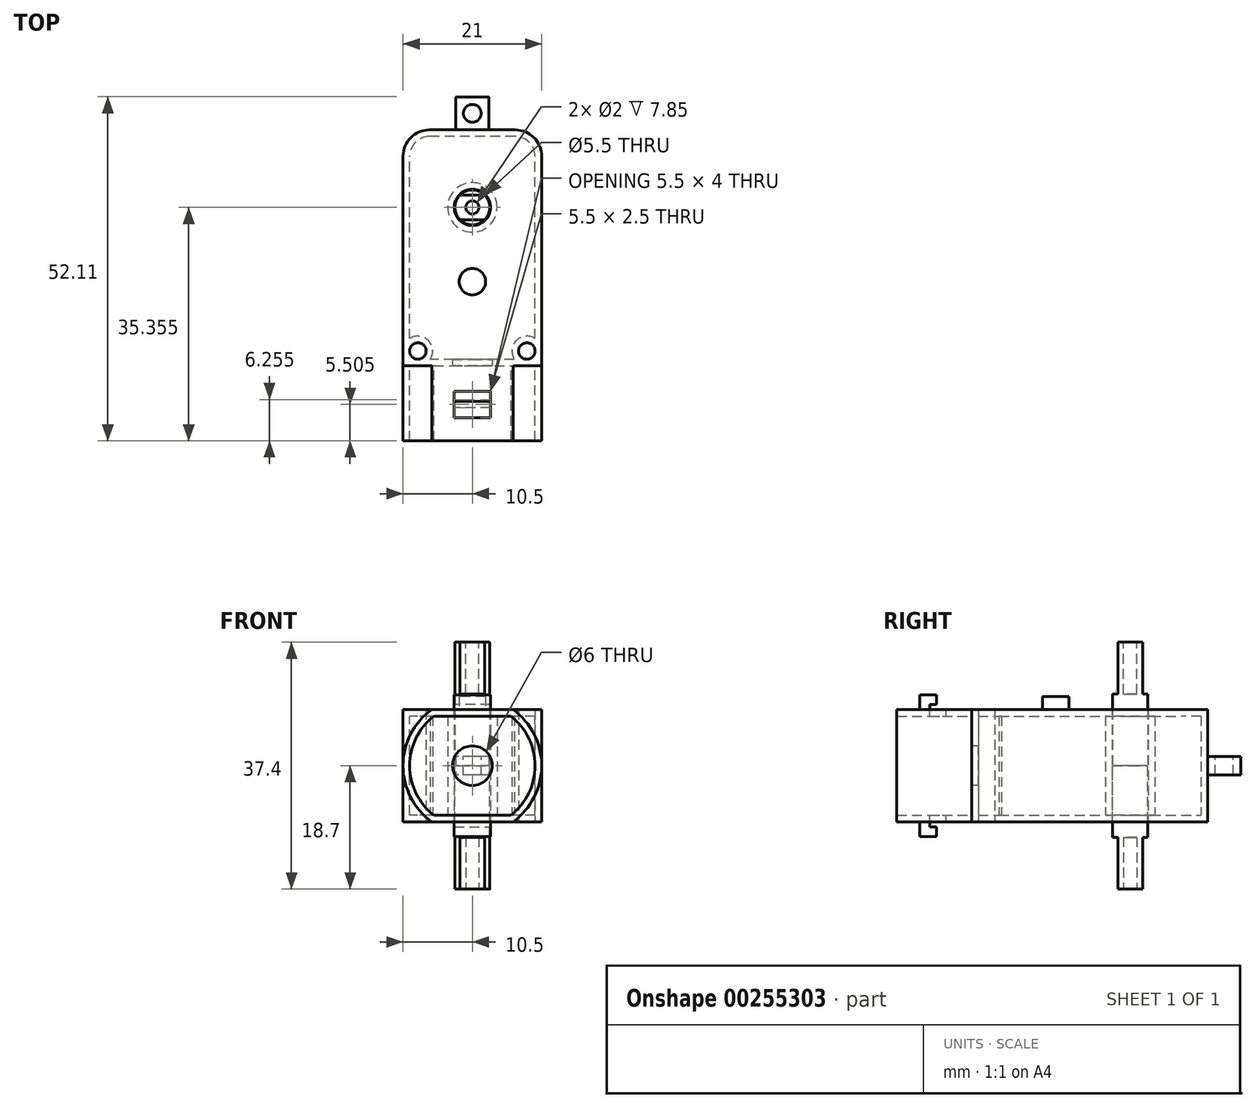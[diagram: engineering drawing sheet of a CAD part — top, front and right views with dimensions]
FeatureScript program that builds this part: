
annotation { "Feature Type Name" : "Feature", "Feature Type Description" : "" }
export const myFeature = defineFeature(function(context is Context, id is Id, definition is map)
    precondition{}
    {
        {
            var Q0;
            Q0=qCreatedBy(makeId("Top.planeOp"),FACE);
            var sketch = newSketch(context, id + "F0", { "sketchPlane" : qUnion([Q0])});
            skLineSegment(sketch, "E0.bottom", {"start": v(10.5, -17.88) * mm, "end": v(-10.5, -17.88) * mm});
            skLineSegment(sketch, "E0.top", {"start": v(10.5, 17.88) * mm, "end": v(-10.5, 17.88) * mm});
            skLineSegment(sketch, "E0.left", {"start": v(10.5, -17.88) * mm, "end": v(10.5, 17.88) * mm});
            skLineSegment(sketch, "E0.right", {"start": v(-10.5, -17.88) * mm, "end": v(-10.5, 17.88) * mm});
            skPoint(sketch, "E0.middle", {"position": v(0, 0) * mm});
            skCircle(sketch, "E1", {"center": v(0, 6.12) * mm, "radius": 2.75 * mm});
            skLineSegment(sketch, "E2", {"start": v(0, 8.88) * mm, "end": v(0, 17.88) * mm});
            skCircle(sketch, "E3", {"center": v(0, -5.13) * mm, "radius": 2 * mm});
            skLineSegment(sketch, "E4", {"start": v(0, 3.37) * mm, "end": v(0, -3.13) * mm});
            skCircle(sketch, "E5", {"center": v(-8.25, -15.63) * mm, "radius": 1.25 * mm});
            skLineSegment(sketch, "E6", {"start": v(-8.25, -16.88) * mm, "end": v(-8.25, -17.88) * mm});
            skLineSegment(sketch, "E7", {"start": v(-9.5, -15.63) * mm, "end": v(-10.5, -15.63) * mm});
            skLineSegment(sketch, "E8", {"start": v(0, -7.13) * mm, "end": v(0, -17.88) * mm});
            skCircle(sketch, "E9.MirrorC", {"center": v(8.25, -15.62) * mm, "radius": 1.25 * mm});
            skSolve(sketch);
        }
        {
            var Q0;
            {var subQ3=sQuery(id+"F0.wireOp",EDGE,"E2");Q0=makeQuery(id+"F0.imprint","IMPRINT",FACE,{"disambiguationData":[TD([[makeQuery(id+"F0.imprint","IMPRINT",EDGE,{"derivedFrom":subQ3}),1.0]])]});}
            var Q1;
            {var subQ3=sQuery(id+"F0.wireOp",EDGE,"E0.left");Q1=makeQuery(id+"F0.imprint","IMPRINT",FACE,{"disambiguationData":[TD([[makeQuery(id+"F0.imprint","IMPRINT",EDGE,{"derivedFrom":subQ3}),1.0]])]});}
            var Q2;
            {var subQ0=sQuery(id+"F0.wireOp",EDGE,"E6");Q2=makeQuery(id+"F0.imprint","IMPRINT",FACE,{"disambiguationData":[TD([[makeQuery(id+"F0.imprint","IMPRINT",EDGE,{"derivedFrom":subQ0}),-1.0]])]});}
            var Q3;
            {var subQ0=sQuery(id+"F0.wireOp",EDGE,"E3");var subQ1=makeQuery(id+"F0.imprint","INTERSECT",VERTEX,{"derivedFrom":[subQ0,sQuery(id+"F0.wireOp",EDGE,"E4")]});Q3=makeQuery(id+"F0.imprint","IMPRINT",FACE,{"disambiguationData":[TD([[makeQuery(id+"F0.imprint","IMPRINT",EDGE,{"disambiguationData":[TD([[subQ1,-1.0]])],"derivedFrom":subQ0}),1.0]])]});}
            extrude(context, id + "F1", {"entities" : qUnion([Q0, Q1, Q2, Q3]), "endBound" : BoundingType.SYMMETRIC, "depth" : 17 * mm});
        }
        {
            var Q0;
            Q0=makeQuery(id+"F1.opExtrude","SWEPT_EDGE",EDGE,{"disambiguationData":[OSD([sQuery(id+"F0.wireOp",EDGE,"E0.top"),sQuery(id+"F0.wireOp",EDGE,"E0.right")])]});
            var Q1;
            Q1=makeQuery(id+"F1.opExtrude","SWEPT_EDGE",EDGE,{"disambiguationData":[OSD([sQuery(id+"F0.wireOp",EDGE,"E0.top"),sQuery(id+"F0.wireOp",EDGE,"E0.left")])]});
            fillet(context, id + "F2", {"entities" : qUnion([Q0, Q1]), "radius" : 4 * mm, "tangentPropagation" : true, "allowEdgeOverflow" : false});
        }
        {
            var Q0;
            Q0=makeQuery(id+"F1.opExtrude","SWEPT_FACE",FACE,{"disambiguationData":[OSD([sQuery(id+"F0.wireOp",EDGE,"E1")])]});
            var Q1;
            Q1=makeQuery(id+"F1.opExtrude","SWEPT_BODY",BODY,{"disambiguationData":[OSD([sQuery(id+"F0.wireOp",EDGE,"E0.bottom"),sQuery(id+"F0.wireOp",EDGE,"E0.top"),sQuery(id+"F0.wireOp",EDGE,"E0.left"),sQuery(id+"F0.wireOp",EDGE,"E0.right"),sQuery(id+"F0.wireOp",EDGE,"E1"),sQuery(id+"F0.wireOp",EDGE,"E3"),sQuery(id+"F0.wireOp",EDGE,"E5"),sQuery(id+"F0.wireOp",EDGE,"E9.MirrorC")])]});
            shell(context, id + "F3", {"isHollow" : true, "entities" : qUnion([Q0]), "parts" : qUnion([Q1]), "thickness" : 1 * mm});
        }
        {
            var Q0;
            Q0=makeQuery(id+"F1.opExtrude","SWEPT_FACE",FACE,{"disambiguationData":[OSD([sQuery(id+"F0.wireOp",EDGE,"E0.top")])]});
            var sketch = newSketch(context, id + "F4", { "sketchPlane" : qUnion([Q0])});
            skLineSegment(sketch, "E10.bottom", {"start": v(-2.5, 1.4) * mm, "end": v(2.5, 1.4) * mm});
            skLineSegment(sketch, "E10.top", {"start": v(-2.5, -1.4) * mm, "end": v(2.5, -1.4) * mm});
            skLineSegment(sketch, "E10.left", {"start": v(-2.5, 1.4) * mm, "end": v(-2.5, -1.4) * mm});
            skLineSegment(sketch, "E10.right", {"start": v(2.5, 1.4) * mm, "end": v(2.5, -1.4) * mm});
            skPoint(sketch, "E10.middle", {"position": v(0, 0) * mm});
            skSolve(sketch);
        }
        {
            var Q0;
            Q0=qSketchRegion(id+"F4",true);
            extrude(context, id + "F5", {"entities" : qUnion([Q0]), "operationType" : NewBodyOperationType.ADD, "depth" : 5 * mm});
        }
        {
            var Q0;
            Q0=makeQuery(id+"F5.opExtrude","CAP_EDGE",EDGE,{"disambiguationData":[OSD([sQuery(id+"F4.wireOp",EDGE,"E10.right")])],"isStart":false});
            var Q1;
            Q1=makeQuery(id+"F5.opExtrude","CAP_EDGE",EDGE,{"disambiguationData":[OSD([sQuery(id+"F4.wireOp",EDGE,"E10.left")])],"isStart":false});
            var Q2;
            Q2=makeQuery(id+"F5.opExtrude","CAP_EDGE",EDGE,{"disambiguationData":[OSD([sQuery(id+"F4.wireOp",EDGE,"E10.left")])],"isStart":true});
            var Q3;
            Q3=makeQuery(id+"F5.opExtrude","CAP_EDGE",EDGE,{"disambiguationData":[OSD([sQuery(id+"F4.wireOp",EDGE,"E10.right")])],"isStart":true});
            fillet(context, id + "F6", {"entities" : qUnion([Q0, Q1, Q2, Q3]), "radius" : (1 / 8) * mm, "tangentPropagation" : true, "allowEdgeOverflow" : false});
        }
        {
            var Q0;
            Q0=makeQuery(id+"F5.opExtrude","SWEPT_FACE",FACE,{"disambiguationData":[OSD([sQuery(id+"F4.wireOp",EDGE,"E10.bottom")])]});
            var sketch = newSketch(context, id + "F7", { "sketchPlane" : qUnion([Q0])});
            skCircle(sketch, "E11", {"center": v(0, 20.38) * mm, "radius": 1.35 * mm});
            skPoint(sketch, "E11.centerSnap0", {"position": v(-2.5, 20.38) * mm});
            skSolve(sketch);
        }
        {
            var Q0;
            Q0=qSketchRegion(id+"F7",true);
            extrude(context, id + "F8", {"entities" : qUnion([Q0]), "operationType" : NewBodyOperationType.REMOVE, "oppositeDirection" : true, "depth" : 2.8 * mm});
        }
        {
            var Q0;
            Q0=makeQuery(id+"F1.opExtrude","SWEPT_FACE",FACE,{"disambiguationData":[OSD([sQuery(id+"F0.wireOp",EDGE,"E0.bottom")])]});
            var sketch = newSketch(context, id + "F9", { "sketchPlane" : qUnion([Q0])});
            skArc(sketch, "E12", {"start": v(-6.16, 8.5) * mm, "mid": v(-10.5, 0) * mm, "end": v(-6.16, -8.5) * mm});
            skLineSegment(sketch, "E13", {"start": v(-6.16, 8.5) * mm, "end": v(6.16, 8.5) * mm});
            skLineSegment(sketch, "E14", {"start": v(-6.16, -8.5) * mm, "end": v(6.16, -8.5) * mm});
            skArc(sketch, "E15.trimOffspring", {"start": v(6.16, -8.5) * mm, "mid": v(10.5, 0) * mm, "end": v(6.16, 8.5) * mm});
            skArc(sketch, "E16", {"start": v(4.24, -8.5) * mm, "mid": v(9.5, 0) * mm, "end": v(4.24, 8.5) * mm});
            skLineSegment(sketch, "E17", {"start": v(-4.24, 8.5) * mm, "end": v(4.24, 8.5) * mm});
            skLineSegment(sketch, "E18", {"start": v(-4.24, -8.5) * mm, "end": v(4.24, -8.5) * mm});
            skArc(sketch, "E19.trimOffspring", {"start": v(-4.24, 8.5) * mm, "mid": v(-9.5, 0) * mm, "end": v(-4.24, -8.5) * mm});
            skLineSegment(sketch, "E20", {"start": v(-5.83, 7.5) * mm, "end": v(5.83, 7.5) * mm});
            skLineSegment(sketch, "E21", {"start": v(-5.83, -7.5) * mm, "end": v(5.83, -7.5) * mm});
            skLineSegment(sketch, "E22", {"start": v(-1.98, -7.5) * mm, "end": v(-1.98, -8.5) * mm});
            skLineSegment(sketch, "E23", {"start": v(-2.47, 7.5) * mm, "end": v(-2.47, 8.5) * mm});
            skSolve(sketch);
        }
        {
            var Q0;
            Q0=qSketchRegion(id+"F9",true);
            extrude(context, id + "F10", {"entities" : qUnion([Q0]), "operationType" : NewBodyOperationType.ADD, "depth" : 11.35 * mm});
        }
        {
            var Q0;
            Q0=makeQuery(id+"F10.boolean.opBoolean","SPLIT",FACE,{"disambiguationData":[TD([makeQuery(id+"F10.opExtrude","SWEPT_FACE",FACE,{"disambiguationData":[OSD([sQuery(id+"F9.wireOp",EDGE,"E16")])]}),makeQuery(id+"F10.opExtrude","SWEPT_FACE",FACE,{"disambiguationData":[OSD([sQuery(id+"F9.wireOp",EDGE,"E19.trimOffspring")])]}),makeQuery(id+"F10.opExtrude","SWEPT_FACE",FACE,{"disambiguationData":[OSD([sQuery(id+"F9.wireOp",EDGE,"E20")])]}),makeQuery(id+"F10.opExtrude","SWEPT_FACE",FACE,{"disambiguationData":[OSD([sQuery(id+"F9.wireOp",EDGE,"E21")])]})])],"derivedFrom":makeQuery(id+"F1.opExtrude","SWEPT_FACE",FACE,{"disambiguationData":[OSD([sQuery(id+"F0.wireOp",EDGE,"E0.bottom")])]})});
            var sketch = newSketch(context, id + "F11", { "sketchPlane" : qUnion([Q0])});
            skCircle(sketch, "E24", {"center": v(0, 0) * mm, "radius": 3 * mm});
            skSolve(sketch);
        }
        {
            var Q0;
            Q0=qSketchRegion(id+"F11",true);
            extrude(context, id + "F12", {"entities" : qUnion([Q0]), "operationType" : NewBodyOperationType.REMOVE, "oppositeDirection" : true, "depth" : 1 * mm});
        }
        {
            var Q0;
            Q0=makeQuery(id+"F10.boolean.opBoolean","MERGE",FACE,{"derivedFrom":[makeQuery(id+"F1.opExtrude","CAP_FACE",FACE,{"disambiguationData":[OSD([sQuery(id+"F0.wireOp",EDGE,"E0.bottom"),sQuery(id+"F0.wireOp",EDGE,"E0.top"),sQuery(id+"F0.wireOp",EDGE,"E0.left"),sQuery(id+"F0.wireOp",EDGE,"E0.right"),sQuery(id+"F0.wireOp",EDGE,"E1"),sQuery(id+"F0.wireOp",EDGE,"E5"),sQuery(id+"F0.wireOp",EDGE,"E9.MirrorC")])],"isStart":false}),makeQuery(id+"F10.opExtrude","SWEPT_FACE",FACE,{"disambiguationData":[OSD([sQuery(id+"F9.wireOp",EDGE,"E13"),sQuery(id+"F9.wireOp",EDGE,"E17")])]})]});
            var sketch = newSketch(context, id + "F13", { "sketchPlane" : qUnion([Q0])});
            skPoint(sketch, "E25.0", {"position": v(0, -5.13) * mm});
            skCircle(sketch, "E26.0", {"center": v(0, -5.13) * mm, "radius": 2 * mm});
            skSolve(sketch);
        }
        {
            var Q0;
            Q0=makeQuery(id+"F13.imprint","IMPRINT",FACE,{"disambiguationData":[TD([[makeQuery(id+"F13.imprint","IMPRINT",EDGE,{"derivedFrom":sQuery(id+"F13.wireOp",EDGE,"E26.0")}),1.0]])]});
            extrude(context, id + "F14", {"entities" : qUnion([Q0]), "operationType" : NewBodyOperationType.ADD, "depth" : 2 * mm});
        }
        {
            var Q0;
            Q0=makeQuery(id+"F10.boolean.opBoolean","MERGE",FACE,{"derivedFrom":[makeQuery(id+"F1.opExtrude","CAP_FACE",FACE,{"disambiguationData":[OSD([sQuery(id+"F0.wireOp",EDGE,"E0.bottom"),sQuery(id+"F0.wireOp",EDGE,"E0.top"),sQuery(id+"F0.wireOp",EDGE,"E0.left"),sQuery(id+"F0.wireOp",EDGE,"E0.right"),sQuery(id+"F0.wireOp",EDGE,"E1"),sQuery(id+"F0.wireOp",EDGE,"E5"),sQuery(id+"F0.wireOp",EDGE,"E9.MirrorC")])],"isStart":false}),makeQuery(id+"F10.opExtrude","SWEPT_FACE",FACE,{"disambiguationData":[OSD([sQuery(id+"F9.wireOp",EDGE,"E13"),sQuery(id+"F9.wireOp",EDGE,"E17")])]})]});
            var sketch = newSketch(context, id + "F15", { "sketchPlane" : qUnion([Q0])});
            skLineSegment(sketch, "E27.bottom", {"start": v(2.75, -24.23) * mm, "end": v(-2.75, -24.23) * mm});
            skLineSegment(sketch, "E27.top", {"start": v(2.75, -21.73) * mm, "end": v(-2.75, -21.73) * mm});
            skLineSegment(sketch, "E27.left", {"start": v(2.75, -24.23) * mm, "end": v(2.75, -21.73) * mm});
            skLineSegment(sketch, "E27.right", {"start": v(-2.75, -24.23) * mm, "end": v(-2.75, -21.73) * mm});
            skPoint(sketch, "E27.middle", {"position": v(0, -22.98) * mm});
            skPoint(sketch, "E27.middle.positionSnap0", {"position": v(0, -29.23) * mm});
            skPoint(sketch, "E27.centerSnap0", {"position": v(0, -29.23) * mm});
            skLineSegment(sketch, "E28", {"start": v(-1.5, -24.23) * mm, "end": v(-1.5, -29.23) * mm});
            skSolve(sketch);
        }
        {
            var Q0;
            Q0=qSketchRegion(id+"F15",true);
            extrude(context, id + "F16", {"entities" : qUnion([Q0]), "operationType" : NewBodyOperationType.REMOVE, "oppositeDirection" : true, "depth" : 25 * mm});
        }
        {
            var Q0;
            Q0=makeQuery(id+"F10.boolean.opBoolean","MERGE",FACE,{"derivedFrom":[makeQuery(id+"F1.opExtrude","CAP_FACE",FACE,{"disambiguationData":[OSD([sQuery(id+"F0.wireOp",EDGE,"E0.bottom"),sQuery(id+"F0.wireOp",EDGE,"E0.top"),sQuery(id+"F0.wireOp",EDGE,"E0.left"),sQuery(id+"F0.wireOp",EDGE,"E0.right"),sQuery(id+"F0.wireOp",EDGE,"E1"),sQuery(id+"F0.wireOp",EDGE,"E5"),sQuery(id+"F0.wireOp",EDGE,"E9.MirrorC")])],"isStart":false}),makeQuery(id+"F10.opExtrude","SWEPT_FACE",FACE,{"disambiguationData":[OSD([sQuery(id+"F9.wireOp",EDGE,"E13"),sQuery(id+"F9.wireOp",EDGE,"E17")])]})]});
            var sketch = newSketch(context, id + "F17", { "sketchPlane" : qUnion([Q0])});
            skPoint(sketch, "E29.0", {"position": v(2.75, -24.23) * mm});
            skLineSegment(sketch, "E30.bottom", {"start": v(-2.75, -24.23) * mm, "end": v(2.75, -24.23) * mm});
            skLineSegment(sketch, "E30.top", {"start": v(-2.75, -25.73) * mm, "end": v(2.75, -25.73) * mm});
            skLineSegment(sketch, "E30.left", {"start": v(-2.75, -24.23) * mm, "end": v(-2.75, -25.73) * mm});
            skLineSegment(sketch, "E30.right", {"start": v(2.75, -24.23) * mm, "end": v(2.75, -25.73) * mm});
            skSolve(sketch);
        }
        {
            var Q0;
            Q0=qSketchRegion(id+"F17",true);
            extrude(context, id + "F18", {"entities" : qUnion([Q0]), "operationType" : NewBodyOperationType.ADD, "depth" : 2.25 * mm});
        }
        {
            var Q0;
            Q0=makeQuery(id+"F18.opExtrude","SWEPT_FACE",FACE,{"disambiguationData":[OSD([sQuery(id+"F17.wireOp",EDGE,"E30.top")])]});
            var sketch = newSketch(context, id + "F19", { "sketchPlane" : qUnion([Q0])});
            skLineSegment(sketch, "E31.bottom", {"start": v(-2.75, 10.75) * mm, "end": v(2.75, 10.75) * mm});
            skLineSegment(sketch, "E31.top", {"start": v(-2.75, 9.25) * mm, "end": v(2.75, 9.25) * mm});
            skLineSegment(sketch, "E31.left", {"start": v(-2.75, 10.75) * mm, "end": v(-2.75, 9.25) * mm});
            skLineSegment(sketch, "E31.right", {"start": v(2.75, 10.75) * mm, "end": v(2.75, 9.25) * mm});
            skSolve(sketch);
        }
        {
            var Q0;
            Q0=qSketchRegion(id+"F19",true);
            extrude(context, id + "F20", {"entities" : qUnion([Q0]), "operationType" : NewBodyOperationType.ADD, "oppositeDirection" : true, "depth" : 2.5 * mm});
        }
        {
            var Q0;
            Q0=makeQuery(id+"F10.boolean.opBoolean","MERGE",FACE,{"derivedFrom":[makeQuery(id+"F1.opExtrude","CAP_FACE",FACE,{"disambiguationData":[OSD([sQuery(id+"F0.wireOp",EDGE,"E0.bottom"),sQuery(id+"F0.wireOp",EDGE,"E0.top"),sQuery(id+"F0.wireOp",EDGE,"E0.left"),sQuery(id+"F0.wireOp",EDGE,"E0.right"),sQuery(id+"F0.wireOp",EDGE,"E1"),sQuery(id+"F0.wireOp",EDGE,"E5"),sQuery(id+"F0.wireOp",EDGE,"E9.MirrorC")])],"isStart":true}),makeQuery(id+"F10.opExtrude","SWEPT_FACE",FACE,{"disambiguationData":[OSD([sQuery(id+"F9.wireOp",EDGE,"E14"),sQuery(id+"F9.wireOp",EDGE,"E18")])]})]});
            var sketch = newSketch(context, id + "F21", { "sketchPlane" : qUnion([Q0])});
            skLineSegment(sketch, "E32.bottom", {"start": v(2.75, 24.23) * mm, "end": v(-2.75, 24.23) * mm});
            skLineSegment(sketch, "E32.top", {"start": v(2.75, 25.73) * mm, "end": v(-2.75, 25.73) * mm});
            skLineSegment(sketch, "E32.left", {"start": v(2.75, 24.23) * mm, "end": v(2.75, 25.73) * mm});
            skLineSegment(sketch, "E32.right", {"start": v(-2.75, 24.23) * mm, "end": v(-2.75, 25.73) * mm});
            skSolve(sketch);
        }
        {
            var Q0;
            Q0=qSketchRegion(id+"F21",true);
            extrude(context, id + "F22", {"entities" : qUnion([Q0]), "operationType" : NewBodyOperationType.ADD, "depth" : 2.25 * mm});
        }
        {
            var Q0;
            Q0=makeQuery(id+"F22.boolean.opBoolean","MERGE",FACE,{"derivedFrom":[makeQuery(id+"F16.boolean.opBoolean","COPY",FACE,{"disambiguationData":[TD([makeQuery(id+"F10.opExtrude","SWEPT_FACE",FACE,{"disambiguationData":[OSD([sQuery(id+"F9.wireOp",EDGE,"E21")])]})])],"derivedFrom":makeQuery(id+"F16.opExtrude","SWEPT_FACE",FACE,{"disambiguationData":[OSD([sQuery(id+"F15.wireOp",EDGE,"E27.bottom")])]})}),makeQuery(id+"F22.opExtrude","SWEPT_FACE",FACE,{"disambiguationData":[OSD([sQuery(id+"F21.wireOp",EDGE,"E32.bottom")])]})]});
            var sketch = newSketch(context, id + "F23", { "sketchPlane" : qUnion([Q0])});
            skLineSegment(sketch, "E33.bottom", {"start": v(2.75, -10.75) * mm, "end": v(-2.75, -10.75) * mm});
            skLineSegment(sketch, "E33.top", {"start": v(2.75, -9.25) * mm, "end": v(-2.75, -9.25) * mm});
            skLineSegment(sketch, "E33.left", {"start": v(2.75, -10.75) * mm, "end": v(2.75, -9.25) * mm});
            skLineSegment(sketch, "E33.right", {"start": v(-2.75, -10.75) * mm, "end": v(-2.75, -9.25) * mm});
            skSolve(sketch);
        }
        {
            var Q0;
            Q0=qSketchRegion(id+"F23",true);
            extrude(context, id + "F24", {"entities" : qUnion([Q0]), "operationType" : NewBodyOperationType.ADD, "depth" : 1 * mm});
        }
        {
            var Q0;
            {var subQ3=sQuery(id+"F0.wireOp",EDGE,"E0.left");Q0=makeQuery(id+"F0.imprint","IMPRINT",FACE,{"disambiguationData":[TD([[makeQuery(id+"F0.imprint","IMPRINT",EDGE,{"derivedFrom":subQ3}),1.0]])]});}
            var sketch = newSketch(context, id + "F25", { "sketchPlane" : qUnion([Q0])});
            skCircle(sketch, "E34.0", {"center": v(0, 6.12) * mm, "radius": 2.75 * mm, "construction": true});
            skCircle(sketch, "E35", {"center": v(0, 6.12) * mm, "radius": 2.64 * mm});
            skSolve(sketch);
        }
        {
            var Q0;
            Q0=qSketchRegion(id+"F25",true);
            extrude(context, id + "F26", {"entities" : qUnion([Q0]), "depth" : (37.4 / 2) * mm});
        }
        {
            var Q0;
            Q0=makeQuery(id+"F26.opExtrude","CAP_FACE",FACE,{"disambiguationData":[OSD([sQuery(id+"F25.wireOp",EDGE,"E35")])],"isStart":false});
            var sketch = newSketch(context, id + "F27", { "sketchPlane" : qUnion([Q0])});
            skLineSegment(sketch, "E36", {"start": v(-1.86, 4.25) * mm, "end": v(1.86, 4.25) * mm});
            skLineSegment(sketch, "E37", {"start": v(0, 6.12) * mm, "end": v(-1.71, 6.12) * mm, "construction": true});
            skLineSegment(sketch, "E38.MirrorCS", {"start": v(-1.86, 8) * mm, "end": v(1.86, 8) * mm});
            skCircle(sketch, "E39.0", {"center": v(0, 6.12) * mm, "radius": 2.64 * mm});
            skPoint(sketch, "E40.orphan", {"position": v(-2.7, 4.25) * mm});
            skPoint(sketch, "E41.orphan", {"position": v(-2.7, 8) * mm});
            skPoint(sketch, "E42.orphan", {"position": v(2.7, 8) * mm});
            skPoint(sketch, "E43.orphan", {"position": v(2.7, 4.25) * mm});
            skCircle(sketch, "E44", {"center": v(0, 6.12) * mm, "radius": 1 * mm});
            skSolve(sketch);
        }
        {
            var Q0;
            {var subQ0=sQuery(id+"F27.wireOp",EDGE,"E36");Q0=makeQuery(id+"F27.imprint","IMPRINT",FACE,{"disambiguationData":[TD([[makeQuery(id+"F27.imprint","IMPRINT",EDGE,{"derivedFrom":subQ0}),-1.0]])]});}
            var Q1;
            {var subQ0=sQuery(id+"F27.wireOp",EDGE,"E38.MirrorCS");Q1=makeQuery(id+"F27.imprint","IMPRINT",FACE,{"disambiguationData":[TD([[makeQuery(id+"F27.imprint","IMPRINT",EDGE,{"derivedFrom":subQ0}),1.0]])]});}
            var Q2;
            Q2=makeQuery(id+"F27.imprint","IMPRINT",FACE,{"disambiguationData":[TD([[makeQuery(id+"F27.imprint","IMPRINT",EDGE,{"derivedFrom":sQuery(id+"F27.wireOp",EDGE,"E44")}),1.0]])]});
            extrude(context, id + "F28", {"entities" : qUnion([Q0, Q1, Q2]), "operationType" : NewBodyOperationType.REMOVE, "oppositeDirection" : true, "depth" : 7.85 * mm});
        }
        {
            var Q0;
            Q0=makeQuery(id+"F26.opExtrude","SWEPT_BODY",BODY,{"disambiguationData":[OSD([sQuery(id+"F25.wireOp",EDGE,"E35")])]});
            var Q1;
            Q1=qCreatedBy(makeId("Top.planeOp"),FACE);
            mirror(context, id + "F29", {"operationType" : NewBodyOperationType.ADD, "entities" : qUnion([Q0]), "mirrorPlane" : qUnion([Q1])});
        }
    });
